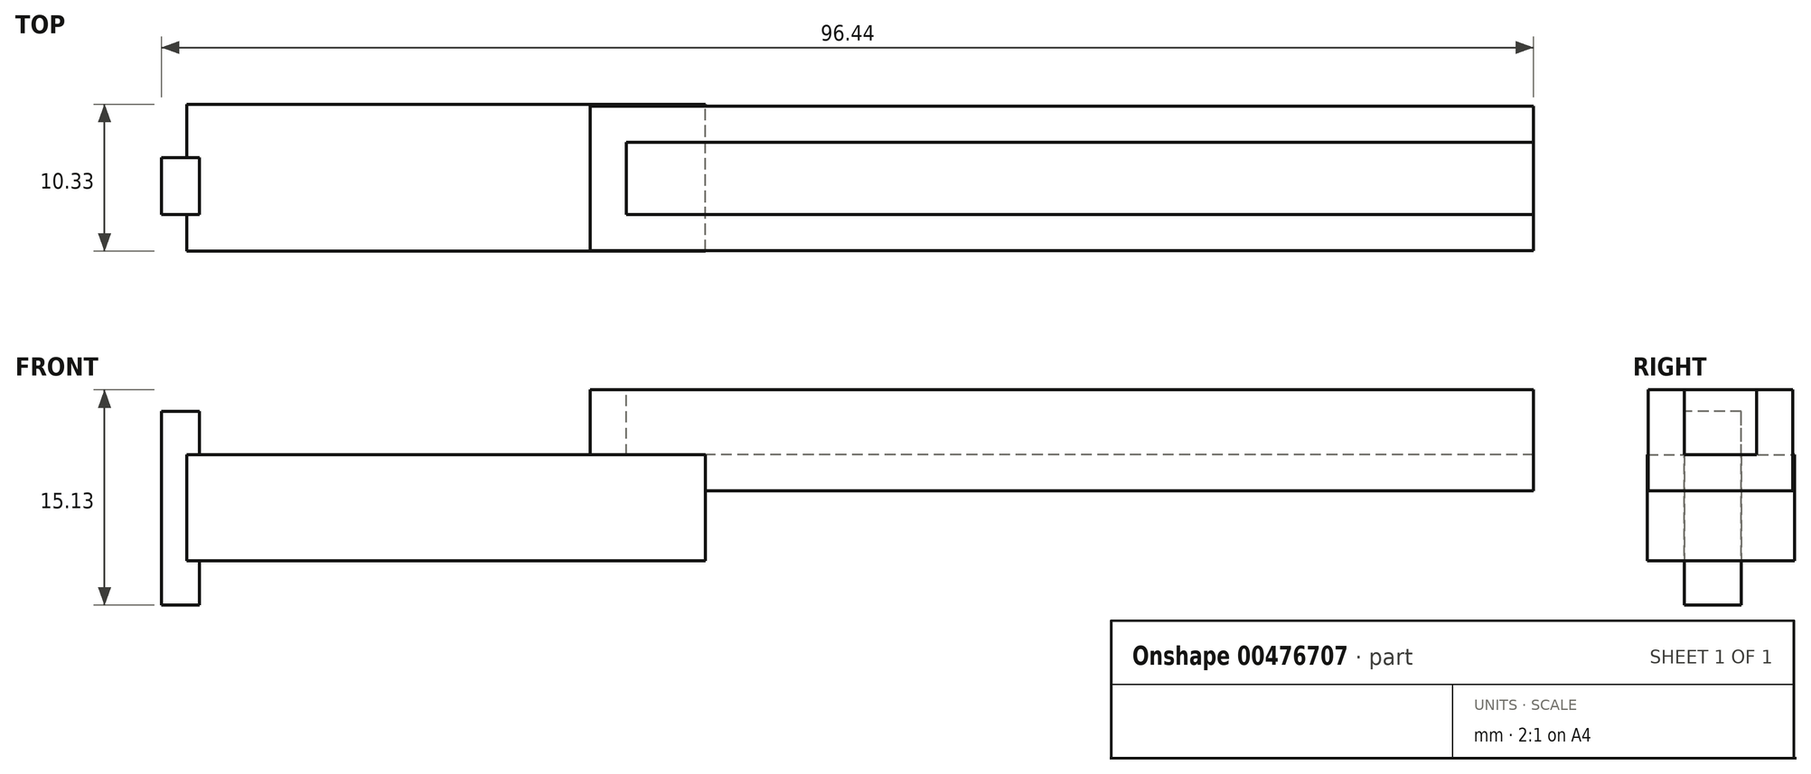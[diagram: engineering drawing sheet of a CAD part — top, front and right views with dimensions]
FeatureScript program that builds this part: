
annotation { "Feature Type Name" : "Feature", "Feature Type Description" : "" }
export const myFeature = defineFeature(function(context is Context, id is Id, definition is map)
    precondition{}
    {
        {
            var Q0;
            Q0=qCreatedBy(makeId("Front.planeOp"),FACE);
            var sketch = newSketch(context, id + "F0", { "sketchPlane" : qUnion([Q0])});
            skLineSegment(sketch, "E0.bottom", {"start": v(58.21, 0) * mm, "end": v(-5.54, 0) * mm});
            skLineSegment(sketch, "E0.top", {"start": v(58.21, 4.57) * mm, "end": v(-5.54, 4.57) * mm});
            skLineSegment(sketch, "E0.left", {"start": v(58.21, 0) * mm, "end": v(58.21, 4.57) * mm});
            skLineSegment(sketch, "E0.right", {"start": v(-5.54, 0) * mm, "end": v(-5.54, 4.57) * mm});
            skSolve(sketch);
        }
        {
            var Q0;
            Q0=qCreatedBy(makeId("Front.planeOp"),FACE);
            var sketch = newSketch(context, id + "F1", { "sketchPlane" : qUnion([Q0])});
            skLineSegment(sketch, "E1.bottom", {"start": v(-5.58, 1.84) * mm, "end": v(-21.76, 1.84) * mm});
            skLineSegment(sketch, "E1.top", {"start": v(-5.58, -2.44) * mm, "end": v(-21.76, -2.44) * mm});
            skLineSegment(sketch, "E1.left", {"start": v(-5.58, 1.84) * mm, "end": v(-5.58, -2.44) * mm});
            skLineSegment(sketch, "E1.right", {"start": v(-21.76, 1.84) * mm, "end": v(-21.76, -2.44) * mm});
            skSolve(sketch);
        }
        {
            var Q0;
            Q0=makeQuery(id+"F0.imprint","IMPRINT",FACE,{"disambiguationData":[TD([[makeQuery(id+"F0.imprint","IMPRINT",EDGE,{"derivedFrom":sQuery(id+"F0.wireOp",EDGE,"E0.bottom")}),-1.0]])]});
            var Q1;
            Q1=makeQuery(id+"F1.imprint","IMPRINT",FACE,{"disambiguationData":[TD([[makeQuery(id+"F1.imprint","IMPRINT",EDGE,{"derivedFrom":sQuery(id+"F1.wireOp",EDGE,"E1.bottom")}),1.0]])]});
            extrude(context, id + "F2", {"entities" : qUnion([Q0, Q1]), "oppositeDirection" : true, "depth" : 5.08 * mm});
        }
        {
            var Q0;
            Q0=makeQuery(id+"F2.opExtrude","SWEPT_FACE",FACE,{"disambiguationData":[OSD([sQuery(id+"F0.wireOp",EDGE,"E0.left")])]});
            var Q1;
            Q1=makeQuery(id+"F2.opExtrude","SWEPT_FACE",FACE,{"disambiguationData":[OSD([sQuery(id+"F0.wireOp",EDGE,"E0.top")])]});
            shell(context, id + "F3", {"entities" : qUnion([Q0, Q1]), "thickness" : 2.54 * mm, "oppositeDirection" : true});
        }
        {
            var Q0;
            Q0=makeQuery(id+"F2.opExtrude","SWEPT_BODY",BODY,{"disambiguationData":[OSD([sQuery(id+"F1.wireOp",EDGE,"E1.bottom"),sQuery(id+"F1.wireOp",EDGE,"E1.top"),sQuery(id+"F1.wireOp",EDGE,"E1.left"),sQuery(id+"F1.wireOp",EDGE,"E1.right")])]});
            deleteBodies(context, id + "F4", {"entities" : qUnion([Q0])});
        }
        {
            var Q0;
            Q0=qCreatedBy(makeId("Right.planeOp"),FACE);
            var sketch = newSketch(context, id + "F5", { "sketchPlane" : qUnion([Q0])});
            skLineSegment(sketch, "E2.bottom", {"start": v(-2.6, 0) * mm, "end": v(7.73, 0) * mm});
            skLineSegment(sketch, "E2.top", {"start": v(-2.6, -7.44) * mm, "end": v(7.73, -7.44) * mm});
            skLineSegment(sketch, "E2.left", {"start": v(-2.6, 0) * mm, "end": v(-2.6, -7.44) * mm});
            skLineSegment(sketch, "E2.right", {"start": v(7.73, 0) * mm, "end": v(7.73, -7.44) * mm});
            skSolve(sketch);
        }
        {
            var Q0;
            Q0=makeQuery(id+"F5.imprint","IMPRINT",FACE,{"disambiguationData":[TD([[makeQuery(id+"F5.imprint","IMPRINT",EDGE,{"derivedFrom":sQuery(id+"F5.wireOp",EDGE,"E2.bottom")}),-1.0]])]});
            extrude(context, id + "F6", {"entities" : qUnion([Q0]), "operationType" : NewBodyOperationType.ADD, "oppositeDirection" : true, "depth" : 36.45 * mm});
        }
        {
            var Q0;
            Q0=qCreatedBy(makeId("Front.planeOp"),FACE);
            var sketch = newSketch(context, id + "F7", { "sketchPlane" : qUnion([Q0])});
            skLineSegment(sketch, "E3.bottom", {"start": v(-35.57, -10.56) * mm, "end": v(-38.23, -10.56) * mm});
            skLineSegment(sketch, "E3.top", {"start": v(-35.57, 3.08) * mm, "end": v(-38.23, 3.08) * mm});
            skLineSegment(sketch, "E3.left", {"start": v(-35.57, -10.56) * mm, "end": v(-35.57, 3.08) * mm});
            skLineSegment(sketch, "E3.right", {"start": v(-38.23, -10.56) * mm, "end": v(-38.23, 3.08) * mm});
            skSolve(sketch);
        }
        {
            var Q0;
            Q0=makeQuery(id+"F7.imprint","IMPRINT",FACE,{"disambiguationData":[TD([[makeQuery(id+"F7.imprint","IMPRINT",EDGE,{"derivedFrom":sQuery(id+"F7.wireOp",EDGE,"E3.bottom")}),-1.0]])]});
            extrude(context, id + "F8", {"entities" : qUnion([Q0]), "operationType" : NewBodyOperationType.ADD, "oppositeDirection" : true, "depth" : 4 * mm});
        }
    });
